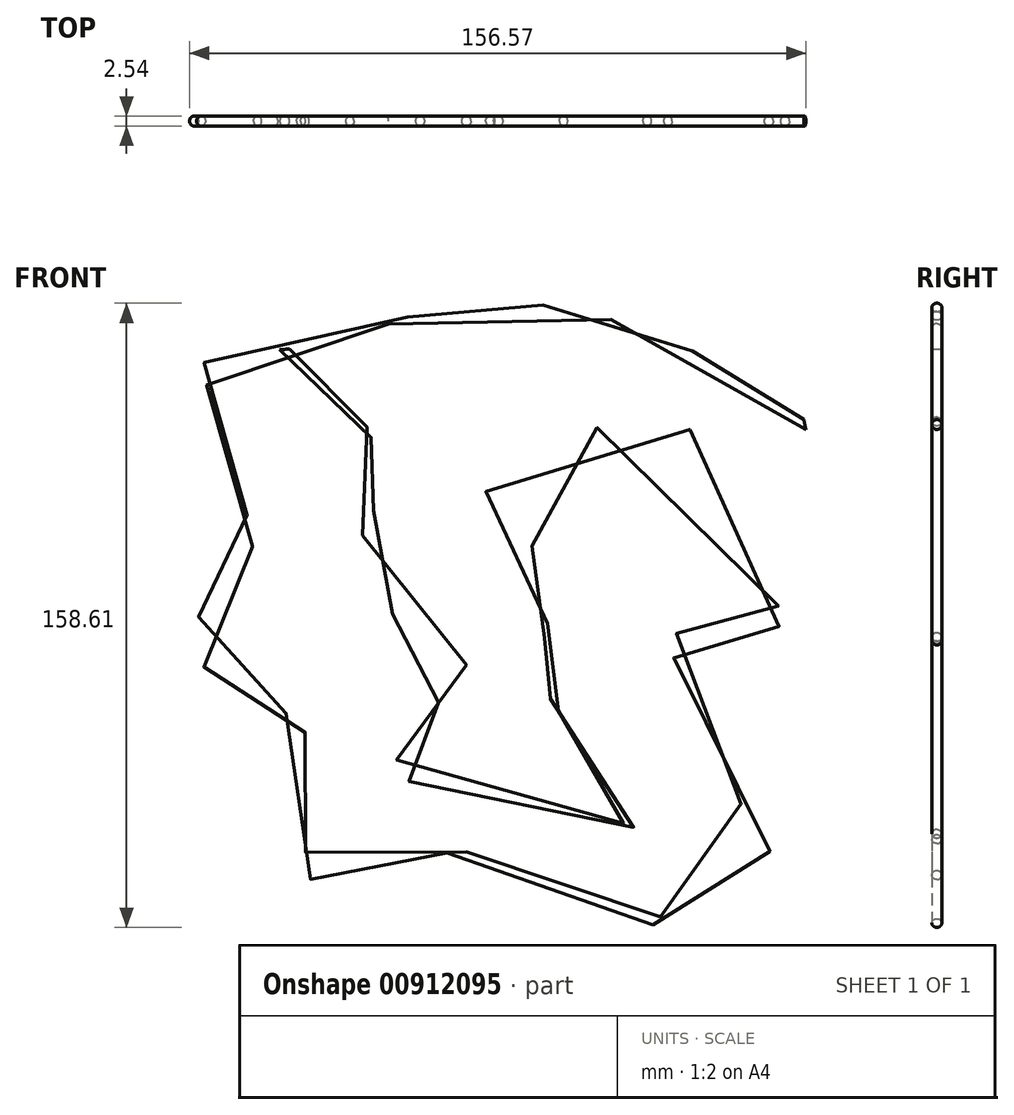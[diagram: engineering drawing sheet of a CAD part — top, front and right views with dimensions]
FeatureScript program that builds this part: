
annotation { "Feature Type Name" : "Feature", "Feature Type Description" : "" }
export const myFeature = defineFeature(function(context is Context, id is Id, definition is map)
    precondition{}
    {
        {
            var Q0;
            Q0=qCreatedBy(makeId("Front.planeOp"),FACE);
            var sketch = newSketch(context, id + "F0", { "sketchPlane" : qUnion([Q0])});
            skFitSpline(sketch, "E0", {"points": [v(-62.13, 64.74) * mm, v(-62.13, 51.16) * mm, v(-27.67, 36.02) * mm, v(-45.42, 12) * mm, v(-15.92, -19.32) * mm, v(-36.55, -35.76) * mm, v(24.54, -57.7) * mm, v(24.54, -33.41) * mm, v(-6.27, -18.01) * mm, v(10.18, 0) * mm, v(-8.35, 29.76) * mm, v(44.12, 41.24) * mm, v(61.08, -6.27) * mm, v(36.29, -8.61) * mm, v(55.34, -51.16) * mm, v(57.17, -77) * mm, v(4.18, -72.3) * mm, v(-34.98, -59.52) * mm, v(-55.34, -67.35) * mm, v(-58.47, -27.93) * mm, v(-83.01, -14.88) * mm, v(-69.96, 14.88) * mm, v(-67.87, 20.88) * mm, v(-80.66, 44.12) * mm, v(-70.48, 69.96) * mm, v(-7.05, 69.7) * mm, v(3.45, 73.84) * mm, v(25.84, 71.27) * mm, v(56.65, 52.2) * mm, v(71, 44.9) * mm], "startDerivative": vector(-303.51, -670.38) * mm, "endDerivative": vector(575.76, -171.01) * mm});
            skSolve(sketch);
        }
        {
            var Q0;
            Q0=sQuery(id+"F0.wireOp",EDGE,"E0");
            var Q1;
            Q1=sQuery(id+"F0.wireOp",VERTEX,"E0.start");
            cPlane(context, id + "F1", {"entities" : qUnion([Q0, Q1]), "cplaneType" : CPlaneType.CURVE_POINT, "offset" : 25.4 * mm, "width" : 152.4 * mm, "height" : 152.4 * mm});
        }
        {
            var Q0;
            Q0=qCreatedBy(id+"F1.planeOp",FACE);
            var sketch = newSketch(context, id + "F2", { "sketchPlane" : qUnion([Q0])});
            skCircle(sketch, "E1", {"center": v(-19.1, 0) * mm, "radius": 1.27 * mm});
            skSolve(sketch);
        }
        {
            var Q0;
            Q0=makeQuery(id+"F2.imprint","IMPRINT",FACE,{"disambiguationData":[TD([[makeQuery(id+"F2.imprint","IMPRINT",EDGE,{"derivedFrom":sQuery(id+"F2.wireOp",EDGE,"E1")}),1.0]])]});
            var Q1;
            Q1=sQuery(id+"F0.wireOp",EDGE,"E0");
            sweep(context, id + "F3", {"profiles" : qUnion([Q0]), "path" : qUnion([Q1])});
        }
    });
